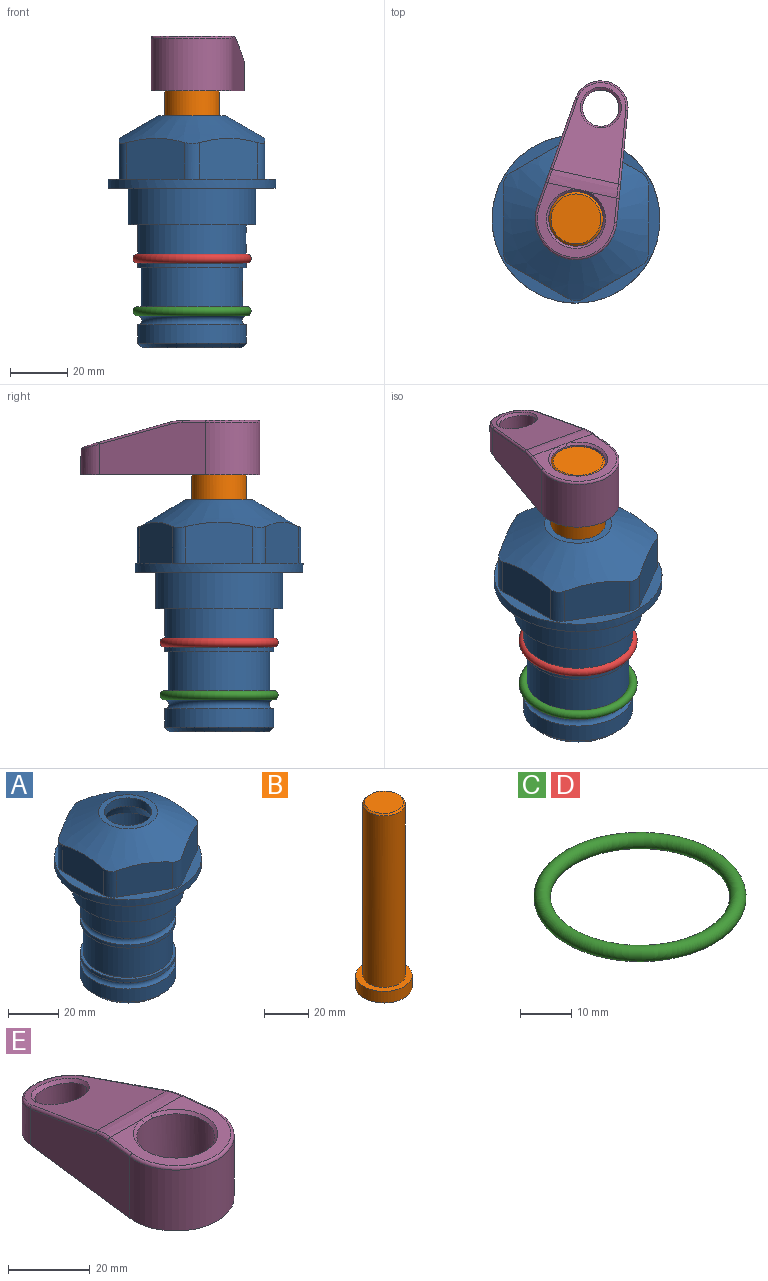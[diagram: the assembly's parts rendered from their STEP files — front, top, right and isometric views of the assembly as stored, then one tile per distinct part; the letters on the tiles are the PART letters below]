
ASSEMBLY  parts=5 mates=3
PART A: 36 faces, bbox 58.7x58.7x81 mm
  f0: cylinder r=17.78mm len=35.56mm, axis (0,0,1), area 1670.8mm2, adj f23,f24,f31
  f1: cylinder r=19.05mm len=38.1mm, axis (0,0,1), area 1191.9mm2, adj f26,f27,f30
  f2: plane 58.66x58.66mm, normal (0,0,-1), area 1150.6mm2, adj f3,f28
  f3: cylinder r=29.33mm len=58.66mm, axis (0,0,-1), area 585.1mm2, adj f2,f4
  f4: plane 58.66x58.66mm, normal (0,0,1), area 475.9mm2, adj f3,f5,f6,f7,f8,f9,f10,f11
  f5: plane 20.32x14.34mm, normal (-0.5,0.87,0), area 324.4mm2, adj f4,f15,f16,f17
  f6: plane 20.32x14.34mm, normal (0.5,0.87,0), area 324.4mm2, adj f4,f14,f15,f17
  f7: plane 23.48x14.34mm, normal (1,0,0), area 324.4mm2, adj f4,f13,f14,f17
  f8: plane 20.32x14.34mm, normal (0.5,-0.87,0), area 324.4mm2, adj f4,f12,f13,f17
  f9: plane 20.32x14.34mm, normal (-0.5,-0.87,0), area 324.4mm2, adj f4,f11,f12,f17
  f10: plane 23.48x14.34mm, normal (-1,0,0), area 324.4mm2, adj f4,f11,f16,f17
  f11: cylinder r=5.08mm len=12.85mm, axis (0,0,-1), area 67.2mm2, adj f4,f9,f10,f17
  f12: cylinder r=5.08mm len=12.85mm, axis (0,0,-1), area 67.2mm2, adj f4,f8,f9,f17
  f13: cylinder r=5.08mm len=12.85mm, axis (0,0,-1), area 67.2mm2, adj f4,f7,f8,f17
  f14: cylinder r=5.08mm len=12.85mm, axis (0,0,-1), area 67.2mm2, adj f4,f6,f7,f17
  f15: cylinder r=5.08mm len=12.85mm, axis (0,0,-1), area 67.2mm2, adj f4,f5,f6,f17
  f16: cylinder r=5.08mm len=12.85mm, axis (0,0,-1), area 67.2mm2, adj f4,f5,f10,f17
  f17: cone r=11.73mm half-angle=60deg, axis (0,0,-1), area 2071.8mm2, adj f5,f6,f7,f8,f9,f10,f11,f12
  f18: plane 23.46x23.46mm, normal (0,0,1), area 147.4mm2, adj f17,f35
  f19: plane 34.93x34.93mm, normal (0,0,-1), area 958mm2, adj f29
  f20: cylinder r=19.05mm len=38.1mm, axis (0,0,1), area 760.1mm2, adj f21,f29
  f21: torus R=19.05mm, axis (0,0,1), area 565.3mm2, adj f20,f22
  f22: cylinder r=19.05mm len=38.1mm, axis (0,0,1), area 190mm2, adj f21,f23
  f23: plane 38.1x38.1mm, normal (0,0,1), area 146.9mm2, adj f0,f22
  f24: plane 38.1x38.1mm, normal (0,0,-1), area 146.9mm2, adj f0,f25
  f25: cylinder r=19.05mm len=38.1mm, axis (0,0,1), area 190mm2, adj f24,f26
  f26: torus R=19.05mm, axis (0,0,1), area 565.3mm2, adj f1,f25
  f27: plane 44.45x44.45mm, normal (0,0,-1), area 411.7mm2, adj f1,f28
  f28: cylinder r=22.23mm len=44.45mm, axis (0,0,1), area 1773.5mm2, adj f2,f27
  f29: cone r=19.05mm half-angle=45deg, axis (0,0,1), area 257.5mm2, adj f19,f20
  f30: cylinder r=3.17mm len=6.75mm, axis (-1,0,0), area 128mm2, adj f1,f33
  f31: cylinder r=3.17mm len=6.35mm, axis (-1,0,0), area 102.5mm2, adj f0,f33
  f32: plane 25.4x25.4mm, normal (0,0,1), area 506.7mm2, adj f33
  f33: cylinder r=12.7mm len=66.42mm, axis (0,0,-1), area 5236.2mm2, adj f30,f31,f32,f34
  f34: cone r=9.53mm half-angle=30deg, axis (0,0,-1), area 443.4mm2, adj f33,f35
  f35: cylinder r=9.53mm len=19.05mm, axis (0,0,-1), area 240.9mm2, adj f18,f34
PART B: 6 faces, bbox 25.4x25.4x101.6 mm
  f0: plane 17.46x17.46mm, normal (0,0,1), area 239.5mm2, adj f5
  f1: plane 25.4x25.4mm, normal (0,0,-1), area 506.7mm2, adj f2
  f2: cylinder r=12.7mm len=25.4mm, axis (0,0,1), area 506.7mm2, adj f1,f3
  f3: plane 25.4x25.4mm, normal (0,0,1), area 221.7mm2, adj f2,f4
  f4: cylinder r=9.53mm len=94.46mm, axis (0,0,1), area 5653mm2, adj f3,f5
  f5: cone r=8.73mm half-angle=45deg, axis (0,0,-1), area 64.4mm2, adj f0,f4
PART C: 1 faces, bbox 44.7x44.7x3.2 mm
  f0: torus R=19.05mm, axis (0,0,1), area 1193.9mm2
PART D: same geometry as C
PART E: 31 faces, bbox 31.7x65.5x19.8 mm
  f0: plane 39.12x18.26mm, normal (0.99,0.12,0), area 612.2mm2, adj f1,f4,f7,f11,f13,f15
  f1: cylinder r=9.53mm len=18.91mm, axis (0,0,-1), area 296.1mm2, adj f0,f2,f7,f17
  f2: plane 39.12x18.26mm, normal (-0.99,0.12,0), area 612.2mm2, adj f1,f4,f7,f12,f14,f16
  f3: cylinder r=6.35mm len=12.7mm, axis (0,0,-1), area 362.4mm2, adj f7,f18
  f4: cylinder r=14.29mm len=28.58mm, axis (0,0,-1), area 882.2mm2, adj f0,f2,f7,f10
  f5: cylinder r=9.53mm len=19.05mm, axis (0,0,-1), area 1092.6mm2, adj f7,f19,f20
  f6: plane 26.99x23.69mm, normal (0,0,1), area 216.2mm2, adj f9,f10,f11,f12,f19
  f7: plane 63.5x28.58mm, normal (0,0,-1), area 661.8mm2, adj f0,f1,f2,f3,f4,f5,f22,f23
  f8: plane 33.52x23.6mm, normal (0,0.26,0.97), area 486mm2, adj f9,f15,f16,f17,f18
  f9: cylinder r=19.05mm len=24.72mm, axis (1,0,0), area 120.4mm2, adj f6,f8,f13,f14,f20
  f10: torus R=13.49mm, axis (0,0,1), area 59mm2, adj f4,f6,f11,f12
  f11: cylinder r=0.79mm len=8.67mm, axis (0.12,-0.99,0), area 10.8mm2, adj f0,f6,f10,f13
  f12: cylinder r=0.79mm len=8.67mm, axis (0.12,0.99,0), area 10.8mm2, adj f2,f6,f10,f14
  f13: bspline ~4.95x1.42mm, area 6.1mm2, adj f0,f9,f11,f15
  f14: bspline ~4.95x1.42mm, area 6.1mm2, adj f2,f9,f12,f16
  f15: cylinder r=0.79mm len=25.95mm, axis (0.12,-0.96,0.26), area 32.9mm2, adj f0,f8,f13,f17
  f16: cylinder r=0.79mm len=25.95mm, axis (0.12,0.96,-0.26), area 32.9mm2, adj f2,f8,f14,f17
  f17: bspline ~18.91x8.38mm, area 30mm2, adj f1,f8,f15,f16
  f18: bspline ~14.29x14.29mm, area 48.3mm2, adj f3,f8
  f19: cone r=9.53mm half-angle=45deg, axis (0,0,1), area 66.5mm2, adj f5,f6,f20
  f20: bspline ~3.22x0.96mm, area 3.5mm2, adj f5,f9,f19
  f21: plane 2.75x2.72mm, normal (0,0,-1), area 2.9mm2, adj f23,f25,f28
  f22: plane 23.05x15.88mm, normal (-0.99,-0.12,0), area 323.6mm2, adj f7,f25,f26,f27,f28,f29
  f23: plane 23.05x15.88mm, normal (0.99,-0.12,0), area 323.6mm2, adj f7,f21,f25,f27,f28,f30
  f24: cylinder r=9.53mm len=10.69mm, axis (0,0,-1), area 114.7mm2, adj f7,f27,f29,f30
  f25: cylinder r=12.7mm len=20.59mm, axis (0,0,-1), area 381.1mm2, adj f7,f21,f22,f23,f26,f28
  f26: plane 2.75x2.72mm, normal (0,0,-1), area 2.9mm2, adj f22,f25,f28
  f27: plane 19.72x18.37mm, normal (0,-0.26,-0.97), area 291.8mm2, adj f22,f23,f24,f28,f29,f30
  f28: cylinder r=15.88mm len=19.92mm, axis (1,0,0), area 54.8mm2, adj f21,f22,f23,f25,f26,f27
  f29: cylinder r=1.59mm len=11mm, axis (0,0,-1), area 34.7mm2, adj f7,f22,f24,f27
  f30: cylinder r=1.59mm len=11mm, axis (0,0,-1), area 34.7mm2, adj f7,f23,f24,f27
PLACE A t=(-5.93,-0.39,15.48)mm fixed
PLACE B rot(axis=(0,0,-1),12.6deg) t=(-5.93,-0.39,4.3)mm
PLACE C t=(-5.93,-0.39,-2.94)mm
PLACE D t=(-5.93,-0.39,15.48)mm
PLACE E rot(axis=(0,0,-1),12.6deg) t=(-5.93,-0.39,5.09)mm
MATE cylindrical B.f2 <-> C.f0  axis (0,0,1) through (-5.93,-0.39,-27.45)mm
MATE fastened B.f2 <-> E.f4  axis (0,0,1) through (-5.93,-0.39,67.8)mm
MATE fastened C.f0 <-> A.f0  axis (0,0,1) through (-5.93,-0.39,-27.45)mm
